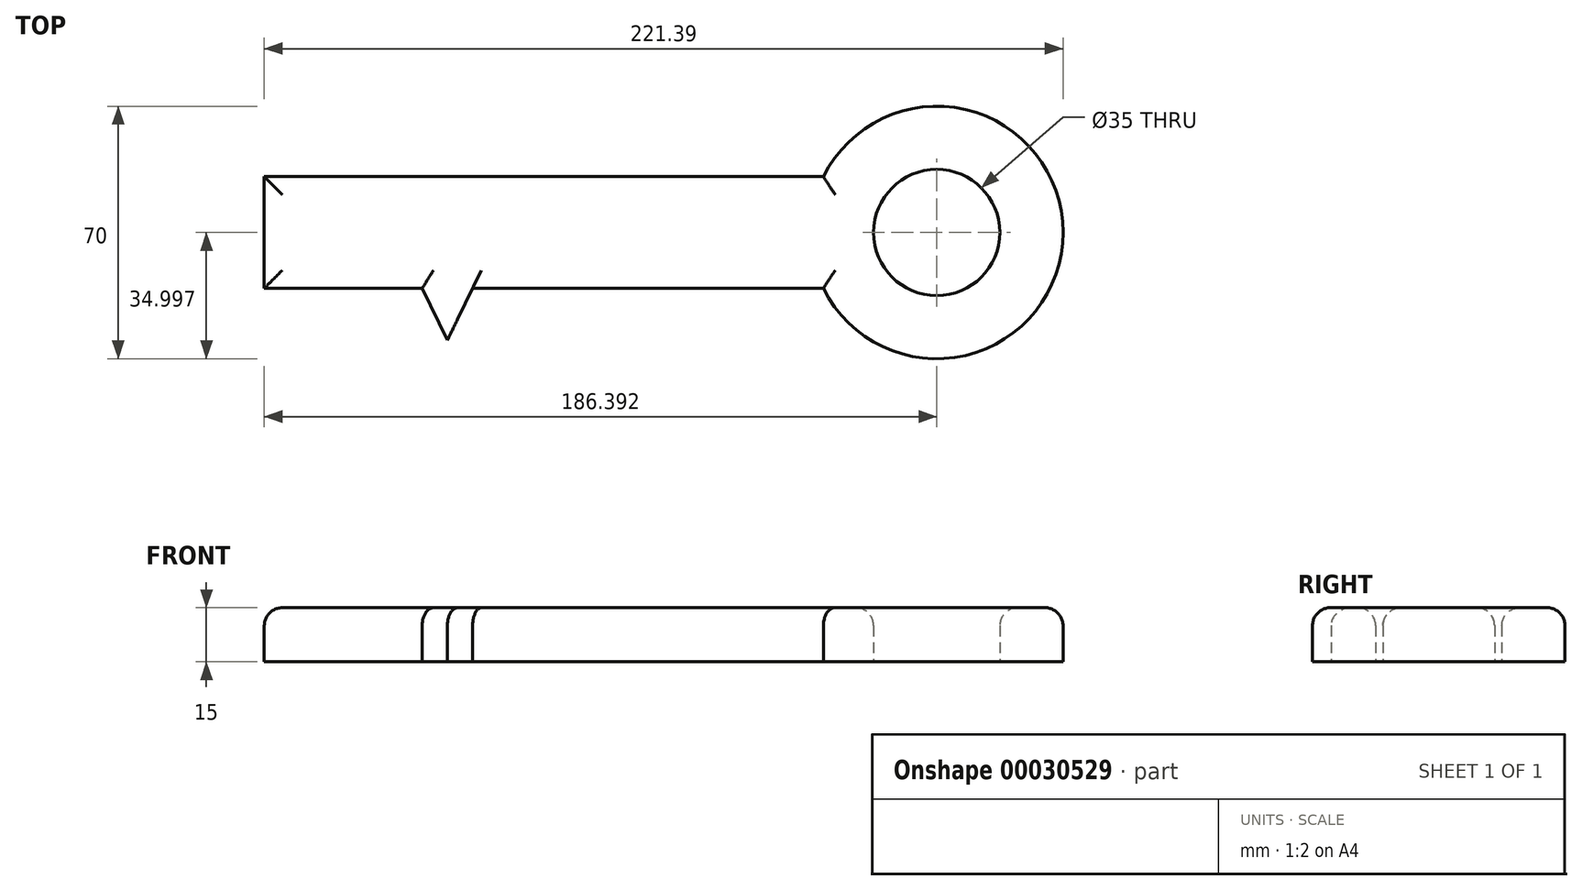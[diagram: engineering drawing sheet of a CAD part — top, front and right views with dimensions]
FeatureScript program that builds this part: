
annotation { "Feature Type Name" : "Feature", "Feature Type Description" : "" }
export const myFeature = defineFeature(function(context is Context, id is Id, definition is map)
    precondition{}
    {
        {
            var Q0;
            Q0=qCreatedBy(makeId("Top.planeOp"),FACE);
            var sketch = newSketch(context, id + "F0", { "sketchPlane" : qUnion([Q0])});
            skLineSegment(sketch, "E0.bottom", {"start": v(-155, 30.95) * mm, "end": v(0, 30.95) * mm});
            skLineSegment(sketch, "E0.top", {"start": v(-155, 0) * mm, "end": v(0, 0) * mm});
            skLineSegment(sketch, "E0.left", {"start": v(-155, 30.95) * mm, "end": v(-155, 0) * mm});
            skLineSegment(sketch, "E1.bottom", {"start": v(-155, 0) * mm, "end": v(-145, 0) * mm});
            skLineSegment(sketch, "E1.top", {"start": v(-155, -30) * mm, "end": v(-145, -30) * mm});
            skLineSegment(sketch, "E1.left", {"start": v(-155, 0) * mm, "end": v(-155, -30) * mm});
            skLineSegment(sketch, "E1.right", {"start": v(-145, 0) * mm, "end": v(-145, -30) * mm});
            skLineSegment(sketch, "E2.bottom", {"start": v(-130.98, 0) * mm, "end": v(-122.98, 0) * mm});
            skLineSegment(sketch, "E2.top", {"start": v(-130.98, -15) * mm, "end": v(-122.98, -15) * mm});
            skLineSegment(sketch, "E2.left", {"start": v(-130.98, 0) * mm, "end": v(-130.98, -15) * mm});
            skLineSegment(sketch, "E2.right", {"start": v(-122.98, 0) * mm, "end": v(-122.98, -15) * mm});
            skLineSegment(sketch, "E3", {"start": v(-111.23, 0) * mm, "end": v(-104.23, -14.38) * mm});
            skLineSegment(sketch, "E4", {"start": v(-97.23, 0) * mm, "end": v(-104.23, -14.38) * mm});
            skArc(sketch, "E5", {"start": v(0, 0) * mm, "mid": v(66.4, 15.48) * mm, "end": v(0, 30.95) * mm});
            skCircle(sketch, "E6", {"center": v(31.4, 15.48) * mm, "radius": 17.5 * mm});
            skLineSegment(sketch, "E7", {"start": v(-155, 15.48) * mm, "end": v(31.4, 15.48) * mm, "construction": true});
            skSolve(sketch);
        }
        {
            var Q0;
            Q0=makeQuery(id+"F0.imprint","IMPRINT",FACE,{"disambiguationData":[TD([[makeQuery(id+"F0.imprint","IMPRINT",EDGE,{"derivedFrom":sQuery(id+"F0.wireOp",EDGE,"E0.bottom")}),-1.0]])]});
            var Q1;
            Q1=makeQuery(id+"F0.imprint","IMPRINT",FACE,{"disambiguationData":[TD([[makeQuery(id+"F0.imprint","IMPRINT",EDGE,{"derivedFrom":sQuery(id+"F0.wireOp",EDGE,"E1.bottom")}),-1.0]])]});
            var Q2;
            Q2=makeQuery(id+"F0.imprint","IMPRINT",FACE,{"disambiguationData":[TD([[makeQuery(id+"F0.imprint","IMPRINT",EDGE,{"derivedFrom":sQuery(id+"F0.wireOp",EDGE,"E2.bottom")}),-1.0]])]});
            var Q3;
            {var subQ1=sQuery(id+"F0.wireOp",EDGE,"E3");Q3=makeQuery(id+"F0.imprint","IMPRINT",FACE,{"disambiguationData":[TD([[makeQuery(id+"F0.imprint","IMPRINT",EDGE,{"derivedFrom":subQ1}),1.0]])]});}
            extrude(context, id + "F1", {"entities" : qUnion([Q0, Q1, Q2, Q3]), "depth" : 15 * mm});
        }
        {
            var Q0;
            Q0=makeQuery(id+"F1.opExtrude","CAP_EDGE",EDGE,{"disambiguationData":[OSD([sQuery(id+"F0.wireOp",EDGE,"E1.top")])],"isStart":false});
            var Q1;
            Q1=makeQuery(id+"F1.opExtrude","CAP_EDGE",EDGE,{"disambiguationData":[OSD([sQuery(id+"F0.wireOp",EDGE,"E0.left"),sQuery(id+"F0.wireOp",EDGE,"E1.left")])],"isStart":false});
            var Q2;
            {var subQ0=sQuery(id+"F0.wireOp",EDGE,"E0.top");Q2=makeQuery(id+"F1.opExtrude","CAP_EDGE",EDGE,{"disambiguationData":[OSD([subQ0]),TDD([makeQuery(id+"F0.imprint","IMPRINT",EDGE,{"disambiguationData":[TD([[makeQuery(id+"F0.imprint","INTERSECT",VERTEX,{"derivedFrom":[subQ0,sQuery(id+"F0.wireOp",EDGE,"E1.bottom"),sQuery(id+"F0.wireOp",EDGE,"E1.right")]}),-1.0]])],"derivedFrom":subQ0})])],"isStart":false});}
            var Q3;
            Q3=makeQuery(id+"F1.opExtrude","CAP_EDGE",EDGE,{"disambiguationData":[OSD([sQuery(id+"F0.wireOp",EDGE,"E2.left")])],"isStart":false});
            var Q4;
            Q4=makeQuery(id+"F1.opExtrude","CAP_EDGE",EDGE,{"disambiguationData":[OSD([sQuery(id+"F0.wireOp",EDGE,"E3")])],"isStart":false});
            var Q5;
            {var subQ0=sQuery(id+"F0.wireOp",EDGE,"E0.top");Q5=makeQuery(id+"F1.opExtrude","CAP_EDGE",EDGE,{"disambiguationData":[OSD([subQ0]),TDD([makeQuery(id+"F0.imprint","IMPRINT",EDGE,{"disambiguationData":[TD([[makeQuery(id+"F0.imprint","INTERSECT",VERTEX,{"derivedFrom":[subQ0,sQuery(id+"F0.wireOp",EDGE,"E3")]}),1.0]])],"derivedFrom":subQ0})])],"isStart":false});}
            var Q6;
            {var subQ0=sQuery(id+"F0.wireOp",EDGE,"E0.top");Q6=makeQuery(id+"F1.opExtrude","CAP_EDGE",EDGE,{"disambiguationData":[OSD([subQ0]),TDD([makeQuery(id+"F0.imprint","IMPRINT",EDGE,{"disambiguationData":[TD([[makeQuery(id+"F0.imprint","INTERSECT",VERTEX,{"derivedFrom":[subQ0,sQuery(id+"F0.wireOp",EDGE,"E5")]}),1.0]])],"derivedFrom":subQ0})])],"isStart":false});}
            var Q7;
            Q7=makeQuery(id+"F1.opExtrude","CAP_EDGE",EDGE,{"disambiguationData":[OSD([sQuery(id+"F0.wireOp",EDGE,"E0.bottom")])],"isStart":false});
            var Q8;
            Q8=makeQuery(id+"F1.opExtrude","CAP_EDGE",EDGE,{"disambiguationData":[OSD([sQuery(id+"F0.wireOp",EDGE,"E5")])],"isStart":false});
            var Q9;
            Q9=makeQuery(id+"F1.opExtrude","CAP_EDGE",EDGE,{"disambiguationData":[OSD([sQuery(id+"F0.wireOp",EDGE,"E6")])],"isStart":false});
            fillet(context, id + "F2", {"entities" : qUnion([Q0, Q1, Q2, Q3, Q4, Q5, Q6, Q7, Q8, Q9]), "radius" : 5 * mm, "tangentPropagation" : true, "allowEdgeOverflow" : false});
        }
    });
